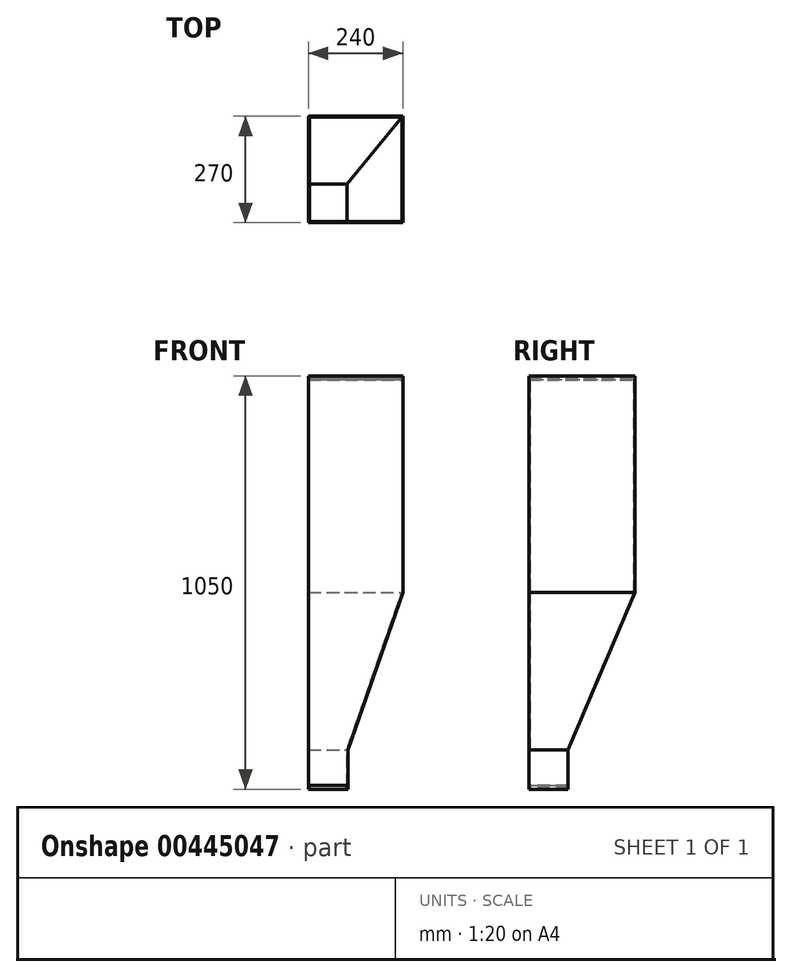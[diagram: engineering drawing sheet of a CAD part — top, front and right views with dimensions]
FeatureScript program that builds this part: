
annotation { "Feature Type Name" : "Feature", "Feature Type Description" : "" }
export const myFeature = defineFeature(function(context is Context, id is Id, definition is map)
    precondition{}
    {
        {
            var Q0;
            Q0=qCreatedBy(makeId("Front.planeOp"),FACE);
            var sketch = newSketch(context, id + "F0", { "sketchPlane" : qUnion([Q0])});
            skLineSegment(sketch, "E0.bottom", {"start": v(0, 0) * mm, "end": v(100, 0) * mm});
            skLineSegment(sketch, "E0.top", {"start": v(0, 100) * mm, "end": v(100, 100) * mm});
            skLineSegment(sketch, "E0.left", {"start": v(0, 0) * mm, "end": v(0, 100) * mm});
            skLineSegment(sketch, "E0.right", {"start": v(100, 0) * mm, "end": v(100, 100) * mm});
            skLineSegment(sketch, "E1", {"start": v(0, 100) * mm, "end": v(0, 500) * mm});
            skLineSegment(sketch, "E2", {"start": v(0, 500) * mm, "end": v(0, 1050) * mm});
            skLineSegment(sketch, "E3", {"start": v(0, 1050) * mm, "end": v(240, 1050) * mm});
            skLineSegment(sketch, "E4", {"start": v(240, 1050) * mm, "end": v(240, 500) * mm});
            skLineSegment(sketch, "E5", {"start": v(240, 500) * mm, "end": v(100, 100) * mm});
            skSolve(sketch);
        }
        {
            var Q0;
            Q0=makeQuery(id+"F0.imprint","IMPRINT",FACE,{"disambiguationData":[TD([[makeQuery(id+"F0.imprint","IMPRINT",EDGE,{"derivedFrom":sQuery(id+"F0.wireOp",EDGE,"E0.top")}),1.0]])]});
            var Q1;
            Q1=makeQuery(id+"F0.imprint","IMPRINT",FACE,{"disambiguationData":[TD([[makeQuery(id+"F0.imprint","IMPRINT",EDGE,{"derivedFrom":sQuery(id+"F0.wireOp",EDGE,"E0.bottom")}),1.0]])]});
            extrude(context, id + "F1", {"entities" : qUnion([Q0, Q1]), "endBound" : BoundingType.SYMMETRIC, "depth" : 270 * mm});
        }
        {
            var Q0;
            Q0=makeQuery(id+"F1.opExtrude","SWEPT_FACE",FACE,{"disambiguationData":[OSD([sQuery(id+"F0.wireOp",EDGE,"E4")])]});
            var sketch = newSketch(context, id + "F2", { "sketchPlane" : qUnion([Q0])});
            skLineSegment(sketch, "E6", {"start": v(135, 500) * mm, "end": v(135, 0) * mm});
            skLineSegment(sketch, "E7", {"start": v(135, 0) * mm, "end": v(-35, 0) * mm});
            skLineSegment(sketch, "E8", {"start": v(-35, 0) * mm, "end": v(-35, 100) * mm});
            skLineSegment(sketch, "E9", {"start": v(-35, 100) * mm, "end": v(135, 500) * mm});
            skSolve(sketch);
        }
        {
            var Q0;
            Q0=makeQuery(id+"F2.imprint","IMPRINT",FACE,{"disambiguationData":[TD([[makeQuery(id+"F2.imprint","IMPRINT",EDGE,{"derivedFrom":sQuery(id+"F2.wireOp",EDGE,"E6")}),-1.0]])]});
            extrude(context, id + "F3", {"entities" : qUnion([Q0]), "operationType" : NewBodyOperationType.REMOVE, "oppositeDirection" : true, "depth" : 240 * mm});
        }
        {
            var Q0;
            Q0=makeQuery(id+"F1.opExtrude","SWEPT_FACE",FACE,{"disambiguationData":[OSD([sQuery(id+"F0.wireOp",EDGE,"E3")])]});
            var Q1;
            Q1=makeQuery(id+"F1.opExtrude","SWEPT_FACE",FACE,{"disambiguationData":[OSD([sQuery(id+"F0.wireOp",EDGE,"E0.bottom")])]});
            shell(context, id + "F4", {"entities" : qUnion([Q0, Q1]), "thickness" : 2.5 * mm});
        }
        {
            var Q0;
            Q0=makeQuery(id+"F1.opExtrude","CAP_FACE",FACE,{"disambiguationData":[OSD([sQuery(id+"F0.wireOp",EDGE,"E0.bottom"),sQuery(id+"F0.wireOp",EDGE,"E0.left"),sQuery(id+"F0.wireOp",EDGE,"E0.right"),sQuery(id+"F0.wireOp",EDGE,"E1"),sQuery(id+"F0.wireOp",EDGE,"E2"),sQuery(id+"F0.wireOp",EDGE,"E3"),sQuery(id+"F0.wireOp",EDGE,"E4"),sQuery(id+"F0.wireOp",EDGE,"E5")])],"isStart":false});
            var sketch = newSketch(context, id + "F5", { "sketchPlane" : qUnion([Q0])});
            skLineSegment(sketch, "E10", {"start": v(1.5, 0) * mm, "end": v(98.5, 0) * mm});
            skLineSegment(sketch, "E11", {"start": v(98.5, 0) * mm, "end": v(98.5, 5) * mm});
            skLineSegment(sketch, "E12", {"start": v(98.5, 5) * mm, "end": v(99.5, 5) * mm});
            skLineSegment(sketch, "E13", {"start": v(99.5, 5) * mm, "end": v(99.5, 10) * mm});
            skLineSegment(sketch, "E14", {"start": v(99.5, 10) * mm, "end": v(0.5, 10) * mm});
            skLineSegment(sketch, "E15", {"start": v(0.5, 10) * mm, "end": v(0.5, 5) * mm});
            skLineSegment(sketch, "E16", {"start": v(1.5, 0) * mm, "end": v(1.5, 5) * mm});
            skLineSegment(sketch, "E17", {"start": v(1.5, 5) * mm, "end": v(0.5, 5) * mm});
            skSolve(sketch);
        }
        {
            var Q0;
            Q0=makeQuery(id+"F5.imprint","IMPRINT",FACE,{"disambiguationData":[TD([[makeQuery(id+"F5.imprint","IMPRINT",EDGE,{"derivedFrom":sQuery(id+"F5.wireOp",EDGE,"E10")}),1.0]])]});
            extrude(context, id + "F6", {"entities" : qUnion([Q0]), "operationType" : NewBodyOperationType.REMOVE, "oppositeDirection" : true, "depth" : 98.5 * mm});
        }
        {
            var Q0;
            Q0=makeQuery(id+"F1.opExtrude","CAP_FACE",FACE,{"disambiguationData":[OSD([sQuery(id+"F0.wireOp",EDGE,"E0.bottom"),sQuery(id+"F0.wireOp",EDGE,"E0.left"),sQuery(id+"F0.wireOp",EDGE,"E0.right"),sQuery(id+"F0.wireOp",EDGE,"E1"),sQuery(id+"F0.wireOp",EDGE,"E2"),sQuery(id+"F0.wireOp",EDGE,"E3"),sQuery(id+"F0.wireOp",EDGE,"E4"),sQuery(id+"F0.wireOp",EDGE,"E5")])],"isStart":true});
            var sketch = newSketch(context, id + "F7", { "sketchPlane" : qUnion([Q0])});
            skLineSegment(sketch, "E18.bottom", {"start": v(-237.5, 1050) * mm, "end": v(-2.5, 1050) * mm});
            skLineSegment(sketch, "E18.top", {"start": v(-237.5, 1045) * mm, "end": v(-2.5, 1045) * mm});
            skLineSegment(sketch, "E18.left", {"start": v(-237.5, 1050) * mm, "end": v(-237.5, 1045) * mm});
            skLineSegment(sketch, "E18.right", {"start": v(-2.5, 1050) * mm, "end": v(-2.5, 1045) * mm});
            skLineSegment(sketch, "E19.bottom", {"start": v(-239, 1045) * mm, "end": v(-1, 1045) * mm});
            skLineSegment(sketch, "E19.top", {"start": v(-239, 1040) * mm, "end": v(-1, 1040) * mm});
            skLineSegment(sketch, "E19.left", {"start": v(-239, 1045) * mm, "end": v(-239, 1040) * mm});
            skLineSegment(sketch, "E19.right", {"start": v(-1, 1045) * mm, "end": v(-1, 1040) * mm});
            skSolve(sketch);
        }
        {
            var Q0;
            Q0=makeQuery(id+"F7.imprint","IMPRINT",FACE,{"disambiguationData":[TD([[makeQuery(id+"F7.imprint","IMPRINT",EDGE,{"derivedFrom":sQuery(id+"F7.wireOp",EDGE,"E18.bottom")}),1.0]])]});
            extrude(context, id + "F8", {"entities" : qUnion([Q0]), "operationType" : NewBodyOperationType.REMOVE, "oppositeDirection" : true, "depth" : 2.5 * mm});
        }
        {
            var Q0;
            Q0=makeQuery(id+"F7.imprint","IMPRINT",FACE,{"disambiguationData":[TD([[makeQuery(id+"F7.imprint","IMPRINT",EDGE,{"derivedFrom":sQuery(id+"F7.wireOp",EDGE,"E19.top")}),1.0]])]});
            extrude(context, id + "F9", {"entities" : qUnion([Q0]), "operationType" : NewBodyOperationType.REMOVE, "oppositeDirection" : true, "depth" : 269 * mm});
        }
    });
